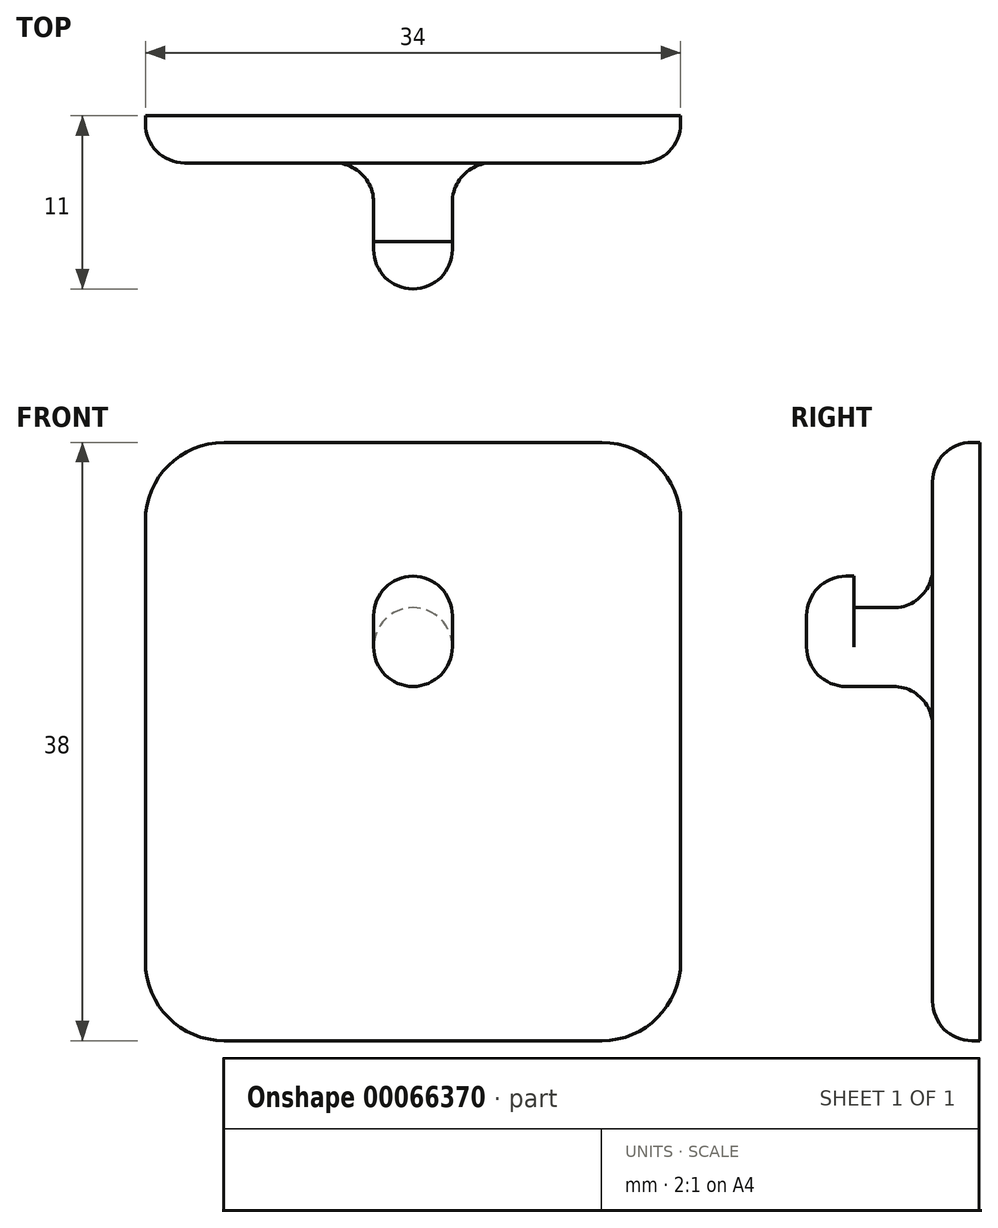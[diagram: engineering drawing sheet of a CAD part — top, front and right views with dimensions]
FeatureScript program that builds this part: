
annotation { "Feature Type Name" : "Feature", "Feature Type Description" : "" }
export const myFeature = defineFeature(function(context is Context, id is Id, definition is map)
    precondition{}
    {
        {
            var Q0;
            Q0=qCreatedBy(makeId("Front.planeOp"),FACE);
            var sketch = newSketch(context, id + "F0", { "sketchPlane" : qUnion([Q0])});
            skLineSegment(sketch, "E0.0", {"start": v(5, 13) * mm, "end": v(29, 13) * mm});
            skArc(sketch, "E1.0", {"start": v(29, 13) * mm, "mid": v(32.54, 11.54) * mm, "end": v(34, 8) * mm});
            skLineSegment(sketch, "E2.0", {"start": v(34, 8) * mm, "end": v(34, -20) * mm});
            skArc(sketch, "E3.0", {"start": v(34, -20) * mm, "mid": v(32.54, -23.54) * mm, "end": v(29, -25) * mm});
            skLineSegment(sketch, "E4.0", {"start": v(29, -25) * mm, "end": v(5, -25) * mm});
            skArc(sketch, "E5.0", {"start": v(5, -25) * mm, "mid": v(1.46, -23.54) * mm, "end": v(0, -20) * mm});
            skLineSegment(sketch, "E6.0", {"start": v(0, -20) * mm, "end": v(0, 8) * mm});
            skArc(sketch, "E7.0", {"start": v(0, 8) * mm, "mid": v(1.46, 11.54) * mm, "end": v(5, 13) * mm});
            skSolve(sketch);
        }
        {
            var Q0;
            Q0 = qSketchRegion(id + "F0", true);
            extrude(context, id + "F1", {"entities" : qUnion([Q0]), "offsetDistance" : 25 * mm, "depth" : 3 * mm});
        }
        {
            var Q0;
            Q0=makeQuery(id+"F1.opExtrude","CAP_FACE",FACE,{"disambiguationData":[OSD([sQuery(id+"F0.wireOp",EDGE,"E0.0"),sQuery(id+"F0.wireOp",EDGE,"E1.0"),sQuery(id+"F0.wireOp",EDGE,"E2.0"),sQuery(id+"F0.wireOp",EDGE,"E3.0"),sQuery(id+"F0.wireOp",EDGE,"E4.0"),sQuery(id+"F0.wireOp",EDGE,"E5.0"),sQuery(id+"F0.wireOp",EDGE,"E6.0"),sQuery(id+"F0.wireOp",EDGE,"E7.0")])],"isStart":false});
            var sketch = newSketch(context, id + "F2", { "sketchPlane" : qUnion([Q0])});
            skArc(sketch, "E8", {"start": v(19.5, 0) * mm, "mid": v(17, 2.5) * mm, "end": v(14.5, 0) * mm});
            skLineSegment(sketch, "E9", {"start": v(14.5, 0) * mm, "end": v(14.5, 0) * mm});
            skLineSegment(sketch, "E10", {"start": v(19.5, 0) * mm, "end": v(19.5, 0) * mm});
            skArc(sketch, "E11", {"start": v(14.5, 0) * mm, "mid": v(17, -2.5) * mm, "end": v(19.5, 0) * mm});
            skSolve(sketch);
        }
        {
            var Q0;
            Q0=makeQuery(id+"F2.imprint","IMPRINT",FACE,{"disambiguationData":[TD([[makeQuery(id+"F2.imprint","IMPRINT",EDGE,{"derivedFrom":sQuery(id+"F2.wireOp",EDGE,"E8")}),1.0]])]});
            extrude(context, id + "F3", {"entities" : qUnion([Q0]), "operationType" : NewBodyOperationType.ADD, "offsetDistance" : 25 * mm, "depth" : 5 * mm});
        }
        {
            var Q0;
            Q0=makeQuery(id+"F3.opExtrude","CAP_FACE",FACE,{"disambiguationData":[OSD([sQuery(id+"F2.wireOp",EDGE,"E8"),sQuery(id+"F2.wireOp",EDGE,"E11")])],"isStart":false});
            var sketch = newSketch(context, id + "F4", { "sketchPlane" : qUnion([Q0])});
            skArc(sketch, "E12.0", {"start": v(19.5, 2) * mm, "mid": v(17, 4.5) * mm, "end": v(14.5, 2) * mm});
            skArc(sketch, "E13.0", {"start": v(14.5, 0) * mm, "mid": v(17, -2.5) * mm, "end": v(19.5, 0) * mm});
            skLineSegment(sketch, "E14", {"start": v(14.5, 2) * mm, "end": v(14.5, 0) * mm});
            skLineSegment(sketch, "E15", {"start": v(19.5, 2) * mm, "end": v(19.5, 0) * mm});
            skSolve(sketch);
        }
        {
            var Q0;
            Q0 = qSketchRegion(id + "F4", true);
            extrude(context, id + "F5", {"entities" : qUnion([Q0]), "operationType" : NewBodyOperationType.ADD, "offsetDistance" : 25 * mm, "depth" : 3 * mm});
        }
        {
            var Q0;
            Q0=makeQuery(id+"F3.opExtrude","CAP_EDGE",EDGE,{"disambiguationData":[OSD([sQuery(id+"F2.wireOp",EDGE,"E8"),sQuery(id+"F2.wireOp",EDGE,"E11")])],"isStart":true});
            var Q1;
            Q1=makeQuery(id+"F5.opExtrude","CAP_EDGE",EDGE,{"disambiguationData":[OSD([sQuery(id+"F4.wireOp",EDGE,"E13.0")])],"isStart":false});
            var Q2;
            Q2=makeQuery(id+"F1.opExtrude","CAP_FACE",FACE,{"disambiguationData":[OSD([sQuery(id+"F0.wireOp",EDGE,"E0.0"),sQuery(id+"F0.wireOp",EDGE,"E1.0"),sQuery(id+"F0.wireOp",EDGE,"E2.0"),sQuery(id+"F0.wireOp",EDGE,"E3.0"),sQuery(id+"F0.wireOp",EDGE,"E4.0"),sQuery(id+"F0.wireOp",EDGE,"E5.0"),sQuery(id+"F0.wireOp",EDGE,"E6.0"),sQuery(id+"F0.wireOp",EDGE,"E7.0")])],"isStart":false});
            fillet(context, id + "F6", {"entities" : qUnion([Q0, Q1, Q2]), "tangentPropagation" : true, "radius" : 2.5 * mm, "defaultsChanged" : false, "vertexSettings" : [], "allowEdgeOverflow" : false});
        }
    });
